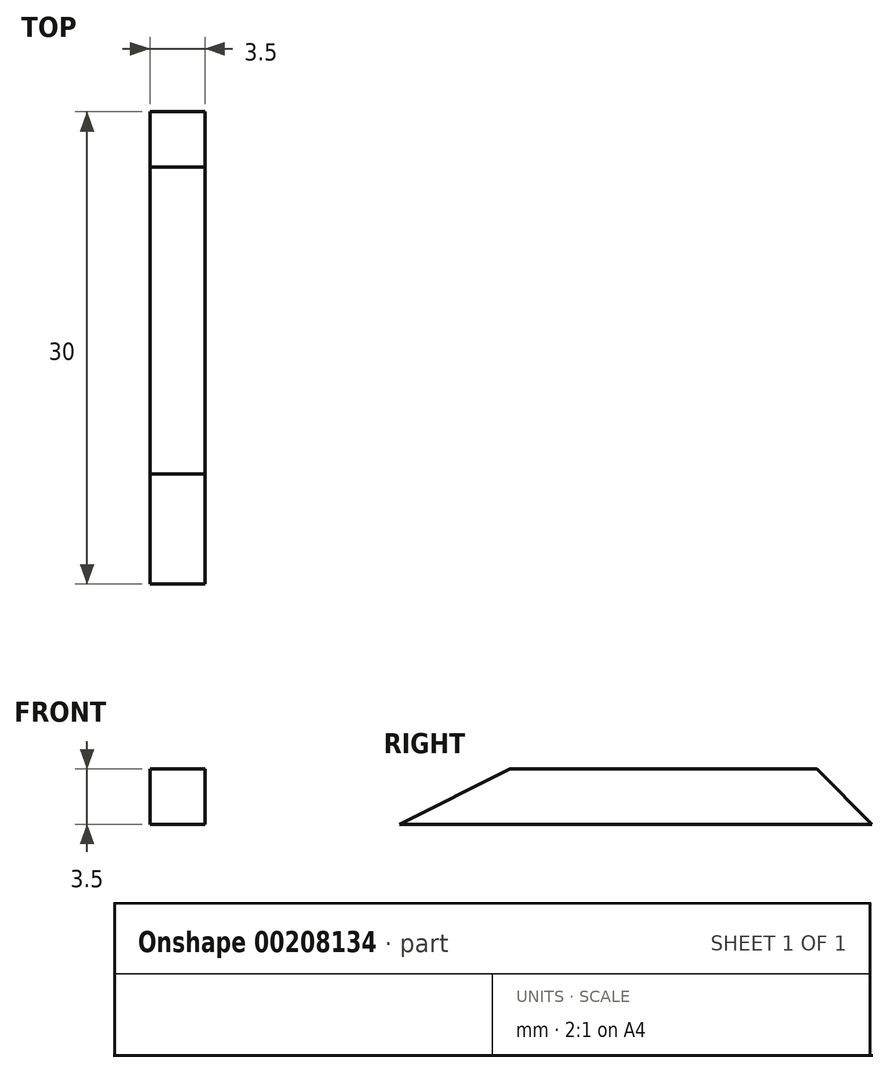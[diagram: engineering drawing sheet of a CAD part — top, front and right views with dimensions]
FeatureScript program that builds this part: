
annotation { "Feature Type Name" : "Feature", "Feature Type Description" : "" }
export const myFeature = defineFeature(function(context is Context, id is Id, definition is map)
    precondition{}
    {
        {
            var Q0;
            Q0=qCreatedBy(makeId("Top.planeOp"),FACE);
            var sketch = newSketch(context, id + "F0", { "sketchPlane" : qUnion([Q0])});
            skLineSegment(sketch, "E0.bottom", {"start": v(-1.75, 15) * mm, "end": v(1.75, 15) * mm});
            skLineSegment(sketch, "E0.top", {"start": v(-1.75, -15) * mm, "end": v(1.75, -15) * mm});
            skLineSegment(sketch, "E0.left", {"start": v(-1.75, 15) * mm, "end": v(-1.75, -15) * mm});
            skLineSegment(sketch, "E0.right", {"start": v(1.75, 15) * mm, "end": v(1.75, -15) * mm});
            skPoint(sketch, "E0.middle", {"position": v(0, 0) * mm});
            skSolve(sketch);
        }
        {
            var Q0;
            Q0 = qSketchRegion(id + "F0", true);
            extrude(context, id + "F1", {"entities" : qUnion([Q0]), "depth" : 3.5 * mm});
        }
        {
            var Q0;
            Q0=makeQuery(id+"F1.opExtrude","SWEPT_FACE",FACE,{"disambiguationData":[OSD([sQuery(id+"F0.wireOp",EDGE,"E0.right")])]});
            var sketch = newSketch(context, id + "F2", { "sketchPlane" : qUnion([Q0])});
            skLineSegment(sketch, "E1", {"start": v(-15, 0) * mm, "end": v(-8, 3.5) * mm});
            skLineSegment(sketch, "E2", {"start": v(-15, 0) * mm, "end": v(-15, 3.5) * mm});
            skLineSegment(sketch, "E3", {"start": v(-15, 3.5) * mm, "end": v(-8, 3.5) * mm});
            skLineSegment(sketch, "E4", {"start": v(11.5, 3.5) * mm, "end": v(15, 0) * mm});
            skLineSegment(sketch, "E5", {"start": v(15, 0) * mm, "end": v(15, 3.5) * mm});
            skLineSegment(sketch, "E6", {"start": v(15, 3.5) * mm, "end": v(11.5, 3.5) * mm});
            skSolve(sketch);
        }
        {
            var Q0;
            Q0 = qSketchRegion(id + "F2", true);
            extrude(context, id + "F3", {"entities" : qUnion([Q0]), "operationType" : NewBodyOperationType.REMOVE, "endBound" : BoundingType.THROUGH_ALL, "oppositeDirection" : true, "depth" : 25.4 * mm});
        }
    });
